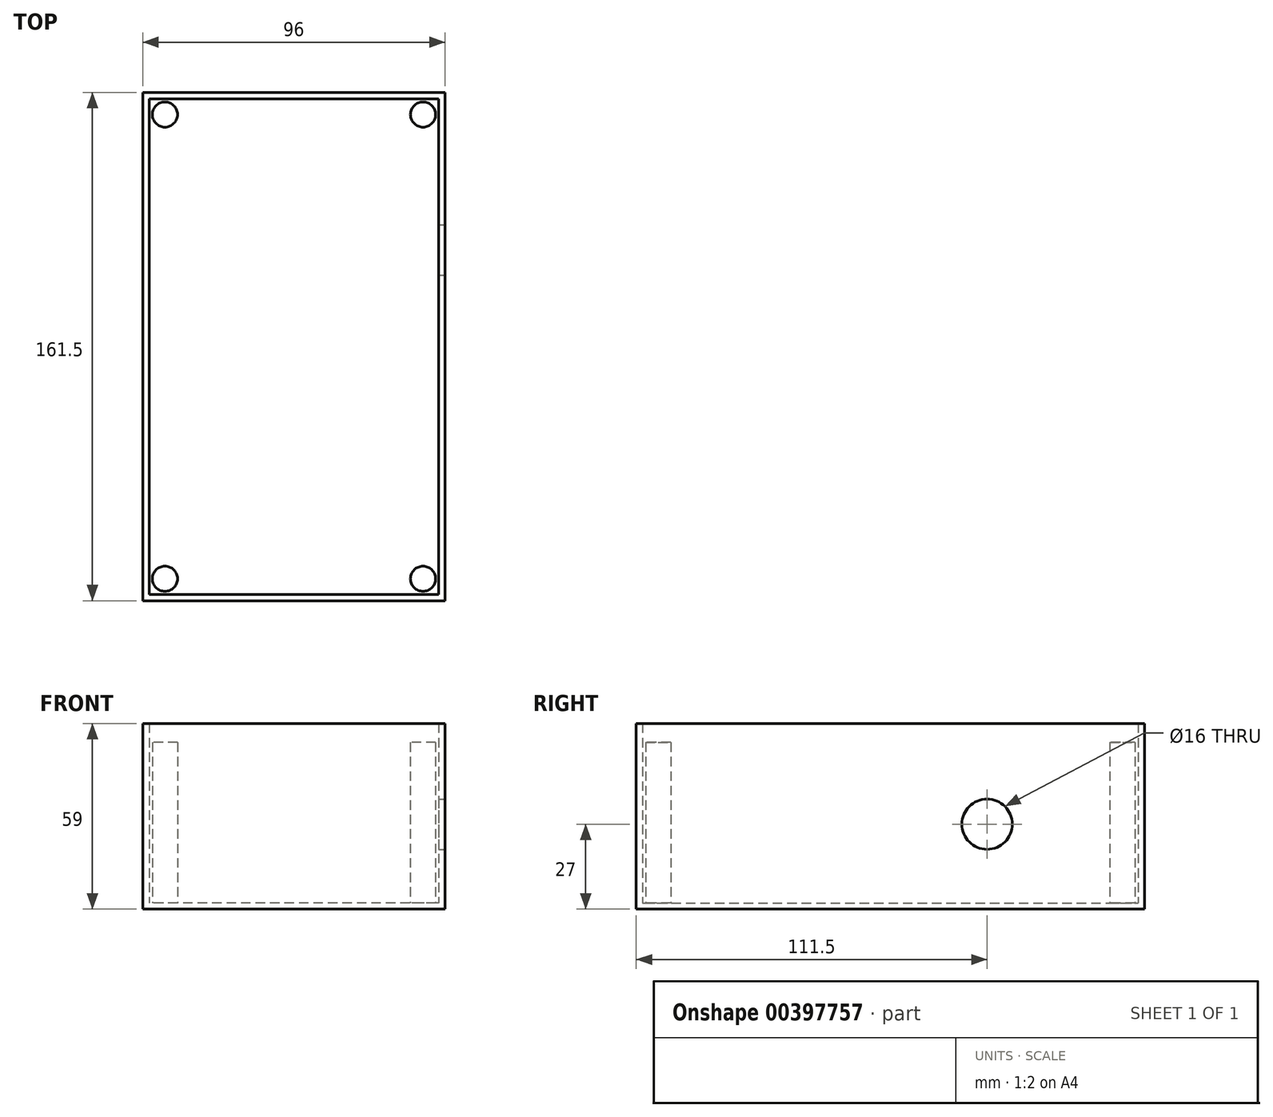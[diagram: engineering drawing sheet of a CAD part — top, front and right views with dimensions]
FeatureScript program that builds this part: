
annotation { "Feature Type Name" : "Feature", "Feature Type Description" : "" }
export const myFeature = defineFeature(function(context is Context, id is Id, definition is map)
    precondition{}
    {
        {
            var Q0;
            Q0=qCreatedBy(makeId("Top.planeOp"),FACE);
            var sketch = newSketch(context, id + "F0", { "sketchPlane" : qUnion([Q0])});
            skLineSegment(sketch, "E0.bottom", {"start": v(48, -80.75) * mm, "end": v(-48, -80.75) * mm});
            skLineSegment(sketch, "E0.top", {"start": v(48, 80.75) * mm, "end": v(-48, 80.75) * mm});
            skLineSegment(sketch, "E0.left", {"start": v(48, -80.75) * mm, "end": v(48, 80.75) * mm});
            skLineSegment(sketch, "E0.right", {"start": v(-48, -80.75) * mm, "end": v(-48, 80.75) * mm});
            skPoint(sketch, "E0.middle", {"position": v(0, 0) * mm});
            skSolve(sketch);
        }
        {
            var Q0;
            Q0 = qSketchRegion(id + "F0", true);
            extrude(context, id + "F1", {"entities" : qUnion([Q0]), "depth" : 59 * mm});
        }
        {
            var Q0;
            Q0=makeQuery(id+"F1.opExtrude","CAP_FACE",FACE,{"disambiguationData":[OSD([sQuery(id+"F0.wireOp",EDGE,"E0.bottom"),sQuery(id+"F0.wireOp",EDGE,"E0.top"),sQuery(id+"F0.wireOp",EDGE,"E0.left"),sQuery(id+"F0.wireOp",EDGE,"E0.right")])],"isStart":false});
            shell(context, id + "F2", {"entities" : qUnion([Q0]), "thickness" : 2 * mm});
        }
        {
            var Q0;
            Q0=makeQuery(id+"F2.opShell","OFFSET_FACE",FACE,{"disambiguationData":[OSD([sQuery(id+"F0.wireOp",EDGE,"E0.bottom"),sQuery(id+"F0.wireOp",EDGE,"E0.top"),sQuery(id+"F0.wireOp",EDGE,"E0.left"),sQuery(id+"F0.wireOp",EDGE,"E0.right")])]});
            var sketch = newSketch(context, id + "F3", { "sketchPlane" : qUnion([Q0])});
            skPoint(sketch, "E1.middle", {"position": v(0, 0) * mm});
            skCircle(sketch, "E2", {"center": v(-41, 73.75) * mm, "radius": 4 * mm});
            skCircle(sketch, "E3", {"center": v(41, 73.75) * mm, "radius": 4 * mm});
            skCircle(sketch, "E4", {"center": v(41, -73.75) * mm, "radius": 4 * mm});
            skCircle(sketch, "E5", {"center": v(-41, -73.75) * mm, "radius": 4 * mm});
            skSolve(sketch);
        }
        {
            var Q0;
            Q0 = qSketchRegion(id + "F3", true);
            extrude(context, id + "F4", {"entities" : qUnion([Q0]), "operationType" : NewBodyOperationType.ADD, "depth" : 51 * mm});
        }
        {
            var Q0;
            Q0=makeQuery(id+"F1.opExtrude","SWEPT_FACE",FACE,{"disambiguationData":[OSD([sQuery(id+"F0.wireOp",EDGE,"E0.left")])]});
            var sketch = newSketch(context, id + "F5", { "sketchPlane" : qUnion([Q0])});
            skCircle(sketch, "E6", {"center": v(30.75, 27) * mm, "radius": 7.75 * mm});
            skSolve(sketch);
        }
        {
            var Q0;
            Q0=sQuery(id+"F5.wireOp",VERTEX,"E6.center");
            var Q1;
            Q1=makeQuery(id+"F1.opExtrude","SWEPT_BODY",BODY,{"disambiguationData":[OSD([sQuery(id+"F0.wireOp",EDGE,"E0.bottom"),sQuery(id+"F0.wireOp",EDGE,"E0.top"),sQuery(id+"F0.wireOp",EDGE,"E0.left"),sQuery(id+"F0.wireOp",EDGE,"E0.right")])]});
            hole(context, id + "F6", {"style" : HoleStyle.SIMPLE, "endStyle" : HoleEndStyle.BLIND, "holeDiameter" : 16 * mm, "holeDepth" : 3 * mm, "isTappedThrough" : true, "tappedDepth" : 12 * mm, "tapClearance" : 3, "locations" : qUnion([Q0]), "scope" : qUnion([Q1])});
        }
    });
